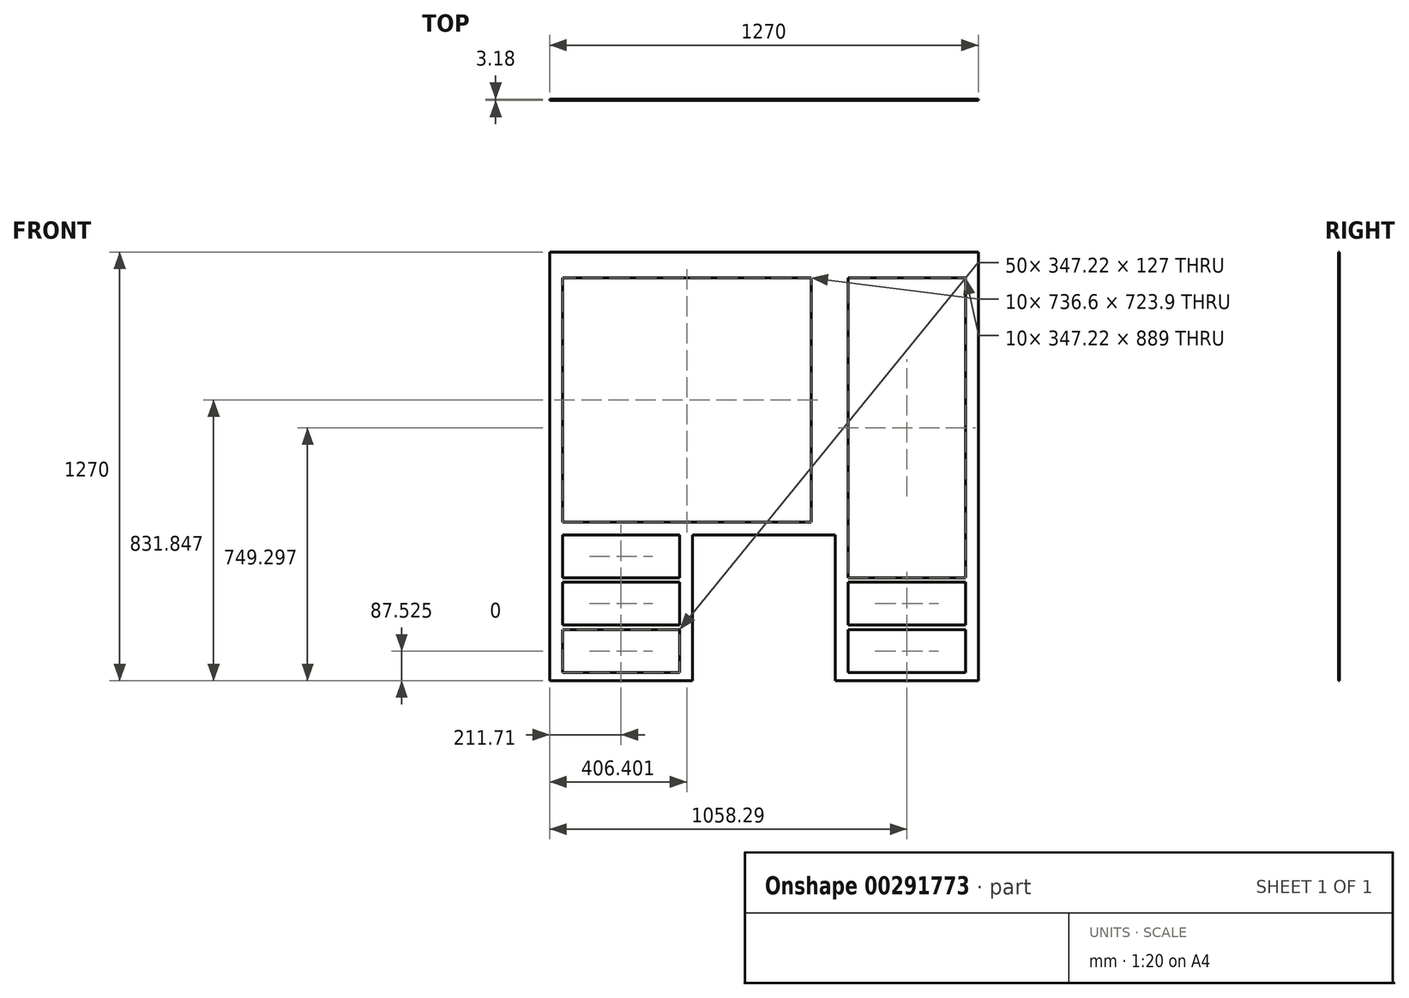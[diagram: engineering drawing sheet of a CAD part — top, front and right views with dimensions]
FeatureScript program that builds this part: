
annotation { "Feature Type Name" : "Feature", "Feature Type Description" : "" }
export const myFeature = defineFeature(function(context is Context, id is Id, definition is map)
    precondition{}
    {
        {
            var Q0;
            Q0=qCreatedBy(makeId("Front.planeOp"),FACE);
            var sketch = newSketch(context, id + "F0", { "sketchPlane" : qUnion([Q0])});
            skLineSegment(sketch, "E0.bottom", {"start": v(-635.49, 722.18) * mm, "end": v(634.51, 722.18) * mm});
            skLineSegment(sketch, "E0.top", {"start": v(-635.49, -547.82) * mm, "end": v(634.51, -547.82) * mm});
            skLineSegment(sketch, "E0.left", {"start": v(-635.49, 722.18) * mm, "end": v(-635.49, -547.82) * mm});
            skLineSegment(sketch, "E0.right", {"start": v(634.51, 722.18) * mm, "end": v(634.51, -547.82) * mm});
            skSolve(sketch);
        }
        {
            var Q0;
            Q0=makeQuery(id+"F0.imprint","IMPRINT",FACE,{"disambiguationData":[TD([[makeQuery(id+"F0.imprint","IMPRINT",EDGE,{"derivedFrom":sQuery(id+"F0.wireOp",EDGE,"E0.bottom")}),-1.0]])]});
            extrude(context, id + "F1", {"entities" : qUnion([Q0]), "endBound" : BoundingType.SYMMETRIC, "depth" : 3.17 * mm});
        }
        {
            var Q0;
            Q0=makeQuery(id+"F1.opExtrude","CAP_FACE",FACE,{"disambiguationData":[OSD([sQuery(id+"F0.wireOp",EDGE,"E0.bottom"),sQuery(id+"F0.wireOp",EDGE,"E0.top"),sQuery(id+"F0.wireOp",EDGE,"E0.left"),sQuery(id+"F0.wireOp",EDGE,"E0.right")])],"isStart":false});
            var sketch = newSketch(context, id + "F2", { "sketchPlane" : qUnion([Q0])});
            skLineSegment(sketch, "E1.bottom", {"start": v(-635.49, 722.18) * mm, "end": v(-635.49, 722.18) * mm});
            skLineSegment(sketch, "E1.top", {"start": v(-635.49, 645.98) * mm, "end": v(-635.49, 645.98) * mm});
            skLineSegment(sketch, "E1.left", {"start": v(-635.49, 722.18) * mm, "end": v(-635.49, 645.98) * mm, "construction": true});
            skLineSegment(sketch, "E1.right", {"start": v(-635.49, 722.18) * mm, "end": v(-635.49, 645.98) * mm, "construction": true});
            skLineSegment(sketch, "E2", {"start": v(-635.49, 722.18) * mm, "end": v(-597.39, 722.18) * mm, "construction": true});
            skLineSegment(sketch, "E3", {"start": v(-597.39, 722.18) * mm, "end": v(-597.39, -547.82) * mm, "construction": true});
            skLineSegment(sketch, "E4", {"start": v(-635.49, -547.82) * mm, "end": v(-212.07, -547.82) * mm, "construction": true});
            skLineSegment(sketch, "E5", {"start": v(634.51, -547.82) * mm, "end": v(211.1, -547.82) * mm, "construction": true});
            skLineSegment(sketch, "E6", {"start": v(-212.07, -547.82) * mm, "end": v(-212.07, -116.02) * mm, "construction": true});
            skLineSegment(sketch, "E7", {"start": v(211.1, -547.82) * mm, "end": v(211.1, -116.02) * mm, "construction": true});
            skLineSegment(sketch, "E8", {"start": v(-212.07, -116.02) * mm, "end": v(211.1, -116.02) * mm, "construction": true});
            skLineSegment(sketch, "E9", {"start": v(634.51, 722.18) * mm, "end": v(596.41, 722.18) * mm, "construction": true});
            skLineSegment(sketch, "E10", {"start": v(596.41, 722.18) * mm, "end": v(596.41, -547.82) * mm, "construction": true});
            skLineSegment(sketch, "E11", {"start": v(-635.49, 645.98) * mm, "end": v(634.51, 645.98) * mm, "construction": true});
            skLineSegment(sketch, "E12", {"start": v(-635.49, -547.82) * mm, "end": v(-635.49, -497.02) * mm, "construction": true});
            skLineSegment(sketch, "E13", {"start": v(-597.39, -497.02) * mm, "end": v(-559.29, -497.02) * mm, "construction": true});
            skLineSegment(sketch, "E14", {"start": v(-212.07, -497.02) * mm, "end": v(-250.17, -497.02) * mm, "construction": true});
            skLineSegment(sketch, "E15", {"start": v(211.1, -497.02) * mm, "end": v(249.2, -497.02) * mm, "construction": true});
            skLineSegment(sketch, "E16", {"start": v(596.41, -497.02) * mm, "end": v(558.31, -497.02) * mm, "construction": true});
            skLineSegment(sketch, "E17", {"start": v(211.1, -116.02) * mm, "end": v(211.1, -77.92) * mm, "construction": true});
            skLineSegment(sketch, "E18", {"start": v(-597.39, 645.98) * mm, "end": v(139.21, 645.98) * mm, "construction": true});
            skLineSegment(sketch, "E19", {"start": v(139.21, 645.98) * mm, "end": v(139.21, -77.92) * mm, "construction": true});
            skLineSegment(sketch, "E20", {"start": v(-597.39, -77.92) * mm, "end": v(139.21, -77.92) * mm, "construction": true});
            skLineSegment(sketch, "E21", {"start": v(211.1, -116.02) * mm, "end": v(249.2, -116.02) * mm, "construction": true});
            skLineSegment(sketch, "E22", {"start": v(-212.07, -116.02) * mm, "end": v(-250.17, -116.02) * mm, "construction": true});
            skLineSegment(sketch, "E23", {"start": v(211.1, 645.98) * mm, "end": v(596.41, 645.98) * mm, "construction": true});
            skLineSegment(sketch, "E24.bottom", {"start": v(-597.39, -116.02) * mm, "end": v(-250.17, -116.02) * mm, "construction": true});
            skLineSegment(sketch, "E24.top", {"start": v(-597.39, -243.02) * mm, "end": v(-250.17, -243.02) * mm, "construction": true});
            skLineSegment(sketch, "E24.left", {"start": v(-597.39, -116.02) * mm, "end": v(-597.39, -243.02) * mm, "construction": true});
            skLineSegment(sketch, "E24.right", {"start": v(-250.17, -116.02) * mm, "end": v(-250.17, -243.02) * mm, "construction": true});
            skLineSegment(sketch, "E25.bottom", {"start": v(249.2, 645.98) * mm, "end": v(596.41, 645.98) * mm, "construction": true});
            skLineSegment(sketch, "E25.top", {"start": v(249.2, -243.02) * mm, "end": v(596.41, -243.02) * mm, "construction": true});
            skLineSegment(sketch, "E25.left", {"start": v(249.2, 645.98) * mm, "end": v(249.2, -243.02) * mm, "construction": true});
            skLineSegment(sketch, "E25.right", {"start": v(596.41, 645.98) * mm, "end": v(596.41, -243.02) * mm, "construction": true});
            skLineSegment(sketch, "E26", {"start": v(-250.17, -243.02) * mm, "end": v(-250.17, -255.72) * mm, "construction": true});
            skLineSegment(sketch, "E27.bottom", {"start": v(-597.39, -255.72) * mm, "end": v(-250.17, -255.72) * mm, "construction": true});
            skLineSegment(sketch, "E27.top", {"start": v(-597.39, -382.72) * mm, "end": v(-250.17, -382.72) * mm, "construction": true});
            skLineSegment(sketch, "E27.left", {"start": v(-597.39, -255.72) * mm, "end": v(-597.39, -382.72) * mm, "construction": true});
            skLineSegment(sketch, "E27.right", {"start": v(-250.17, -255.72) * mm, "end": v(-250.17, -382.72) * mm, "construction": true});
            skLineSegment(sketch, "E28", {"start": v(-250.17, -382.72) * mm, "end": v(-250.17, -396.8) * mm});
            skLineSegment(sketch, "E29.bottom", {"start": v(-250.17, -396.8) * mm, "end": v(-597.39, -396.8) * mm, "construction": true});
            skLineSegment(sketch, "E29.top", {"start": v(-250.17, -523.8) * mm, "end": v(-597.39, -523.8) * mm, "construction": true});
            skLineSegment(sketch, "E29.left", {"start": v(-250.17, -396.8) * mm, "end": v(-250.17, -523.8) * mm, "construction": true});
            skLineSegment(sketch, "E29.right", {"start": v(-597.39, -396.8) * mm, "end": v(-597.39, -523.8) * mm, "construction": true});
            skLineSegment(sketch, "E30", {"start": v(-250.17, -523.8) * mm, "end": v(-250.17, -547.82) * mm, "construction": true});
            skLineSegment(sketch, "E31.bottom", {"start": v(249.2, -255.72) * mm, "end": v(596.41, -255.72) * mm});
            skLineSegment(sketch, "E31.top", {"start": v(249.2, -382.72) * mm, "end": v(596.41, -382.72) * mm});
            skLineSegment(sketch, "E31.left", {"start": v(249.2, -255.72) * mm, "end": v(249.2, -382.72) * mm});
            skLineSegment(sketch, "E31.right", {"start": v(596.41, -255.72) * mm, "end": v(596.41, -382.72) * mm});
            skLineSegment(sketch, "E32.bottom", {"start": v(249.2, -396.8) * mm, "end": v(596.41, -396.8) * mm});
            skLineSegment(sketch, "E32.top", {"start": v(249.2, -523.8) * mm, "end": v(596.41, -523.8) * mm});
            skLineSegment(sketch, "E32.left", {"start": v(249.2, -396.8) * mm, "end": v(249.2, -523.8) * mm});
            skLineSegment(sketch, "E32.right", {"start": v(596.41, -396.8) * mm, "end": v(596.41, -523.8) * mm});
            skLineSegment(sketch, "E33.bottom", {"start": v(-597.39, 645.98) * mm, "end": v(139.21, 645.98) * mm});
            skLineSegment(sketch, "E33.top", {"start": v(-597.39, -77.92) * mm, "end": v(139.21, -77.92) * mm});
            skLineSegment(sketch, "E33.left", {"start": v(-597.39, 645.98) * mm, "end": v(-597.39, -77.92) * mm});
            skLineSegment(sketch, "E33.right", {"start": v(139.21, 645.98) * mm, "end": v(139.21, -77.92) * mm});
            skLineSegment(sketch, "E34.bottom", {"start": v(249.2, 645.98) * mm, "end": v(596.41, 645.98) * mm});
            skLineSegment(sketch, "E34.top", {"start": v(249.2, -243.02) * mm, "end": v(596.41, -243.02) * mm});
            skLineSegment(sketch, "E34.left", {"start": v(249.2, 645.98) * mm, "end": v(249.2, -243.02) * mm});
            skLineSegment(sketch, "E34.right", {"start": v(596.41, 645.98) * mm, "end": v(596.41, -243.02) * mm});
            skLineSegment(sketch, "E35.bottom", {"start": v(-597.39, -116.02) * mm, "end": v(-250.17, -116.02) * mm});
            skLineSegment(sketch, "E35.top", {"start": v(-597.39, -243.02) * mm, "end": v(-250.17, -243.02) * mm});
            skLineSegment(sketch, "E35.left", {"start": v(-597.39, -116.02) * mm, "end": v(-597.39, -243.02) * mm});
            skLineSegment(sketch, "E35.right", {"start": v(-250.17, -116.02) * mm, "end": v(-250.17, -243.02) * mm});
            skLineSegment(sketch, "E36.bottom", {"start": v(-597.39, -255.72) * mm, "end": v(-250.17, -255.72) * mm});
            skLineSegment(sketch, "E36.top", {"start": v(-597.39, -382.72) * mm, "end": v(-250.17, -382.72) * mm});
            skLineSegment(sketch, "E36.left", {"start": v(-597.39, -255.72) * mm, "end": v(-597.39, -382.72) * mm});
            skLineSegment(sketch, "E36.right", {"start": v(-250.17, -255.72) * mm, "end": v(-250.17, -382.72) * mm});
            skLineSegment(sketch, "E37.bottom", {"start": v(-597.39, -396.8) * mm, "end": v(-250.17, -396.8) * mm});
            skLineSegment(sketch, "E37.top", {"start": v(-597.39, -523.8) * mm, "end": v(-250.17, -523.8) * mm});
            skLineSegment(sketch, "E37.left", {"start": v(-597.39, -396.8) * mm, "end": v(-597.39, -523.8) * mm});
            skLineSegment(sketch, "E37.right", {"start": v(-250.17, -396.8) * mm, "end": v(-250.17, -523.8) * mm});
            skLineSegment(sketch, "E38.bottom", {"start": v(-212.07, -116.02) * mm, "end": v(211.1, -116.02) * mm});
            skLineSegment(sketch, "E38.top", {"start": v(-212.07, -547.82) * mm, "end": v(211.1, -547.82) * mm});
            skLineSegment(sketch, "E38.left", {"start": v(-212.07, -116.02) * mm, "end": v(-212.07, -547.82) * mm});
            skLineSegment(sketch, "E38.right", {"start": v(211.1, -116.02) * mm, "end": v(211.1, -547.82) * mm});
            skSolve(sketch);
        }
        {
            var Q0;
            Q0=makeQuery(id+"F2.imprint","IMPRINT",FACE,{"disambiguationData":[TD([[makeQuery(id+"F2.imprint","IMPRINT",EDGE,{"derivedFrom":sQuery(id+"F2.wireOp",EDGE,"E33.bottom")}),-1.0]])]});
            extrude(context, id + "F3", {"entities" : qUnion([Q0]), "operationType" : NewBodyOperationType.REMOVE, "endBound" : BoundingType.THROUGH_ALL, "oppositeDirection" : true, "depth" : 25.4 * mm});
        }
        {
            var Q0;
            Q0=makeQuery(id+"F2.imprint","IMPRINT",FACE,{"disambiguationData":[TD([[makeQuery(id+"F2.imprint","IMPRINT",EDGE,{"derivedFrom":sQuery(id+"F2.wireOp",EDGE,"E34.bottom")}),-1.0]])]});
            extrude(context, id + "F4", {"entities" : qUnion([Q0]), "operationType" : NewBodyOperationType.REMOVE, "endBound" : BoundingType.THROUGH_ALL, "oppositeDirection" : true, "depth" : 25.4 * mm});
        }
        {
            var Q0;
            Q0=makeQuery(id+"F2.imprint","IMPRINT",FACE,{"disambiguationData":[TD([[makeQuery(id+"F2.imprint","IMPRINT",EDGE,{"derivedFrom":sQuery(id+"F2.wireOp",EDGE,"E35.bottom")}),-1.0]])]});
            extrude(context, id + "F5", {"entities" : qUnion([Q0]), "operationType" : NewBodyOperationType.REMOVE, "endBound" : BoundingType.THROUGH_ALL, "oppositeDirection" : true, "depth" : 25.4 * mm});
        }
        {
            var Q0;
            Q0=makeQuery(id+"F2.imprint","IMPRINT",FACE,{"disambiguationData":[TD([[makeQuery(id+"F2.imprint","IMPRINT",EDGE,{"derivedFrom":sQuery(id+"F2.wireOp",EDGE,"E36.bottom")}),-1.0]])]});
            extrude(context, id + "F6", {"entities" : qUnion([Q0]), "operationType" : NewBodyOperationType.REMOVE, "endBound" : BoundingType.THROUGH_ALL, "oppositeDirection" : true, "depth" : 25.4 * mm});
        }
        {
            var Q0;
            Q0=makeQuery(id+"F2.imprint","IMPRINT",FACE,{"disambiguationData":[TD([[makeQuery(id+"F2.imprint","IMPRINT",EDGE,{"derivedFrom":sQuery(id+"F2.wireOp",EDGE,"E37.bottom")}),-1.0]])]});
            extrude(context, id + "F7", {"entities" : qUnion([Q0]), "operationType" : NewBodyOperationType.REMOVE, "endBound" : BoundingType.THROUGH_ALL, "oppositeDirection" : true, "depth" : 25.4 * mm});
        }
        {
            var Q0;
            Q0=makeQuery(id+"F2.imprint","IMPRINT",FACE,{"disambiguationData":[TD([[makeQuery(id+"F2.imprint","IMPRINT",EDGE,{"derivedFrom":sQuery(id+"F2.wireOp",EDGE,"E38.bottom")}),-1.0]])]});
            extrude(context, id + "F8", {"entities" : qUnion([Q0]), "operationType" : NewBodyOperationType.REMOVE, "endBound" : BoundingType.THROUGH_ALL, "oppositeDirection" : true, "depth" : 25.4 * mm});
        }
        {
            var Q0;
            Q0=makeQuery(id+"F2.imprint","IMPRINT",FACE,{"disambiguationData":[TD([[makeQuery(id+"F2.imprint","IMPRINT",EDGE,{"derivedFrom":sQuery(id+"F2.wireOp",EDGE,"E31.bottom")}),-1.0]])]});
            extrude(context, id + "F9", {"entities" : qUnion([Q0]), "operationType" : NewBodyOperationType.REMOVE, "endBound" : BoundingType.THROUGH_ALL, "oppositeDirection" : true, "depth" : 25.4 * mm});
        }
        {
            var Q0;
            Q0=makeQuery(id+"F2.imprint","IMPRINT",FACE,{"disambiguationData":[TD([[makeQuery(id+"F2.imprint","IMPRINT",EDGE,{"derivedFrom":sQuery(id+"F2.wireOp",EDGE,"E32.bottom")}),-1.0]])]});
            extrude(context, id + "F10", {"entities" : qUnion([Q0]), "operationType" : NewBodyOperationType.REMOVE, "endBound" : BoundingType.THROUGH_ALL, "oppositeDirection" : true, "depth" : 25.4 * mm});
        }
    });
